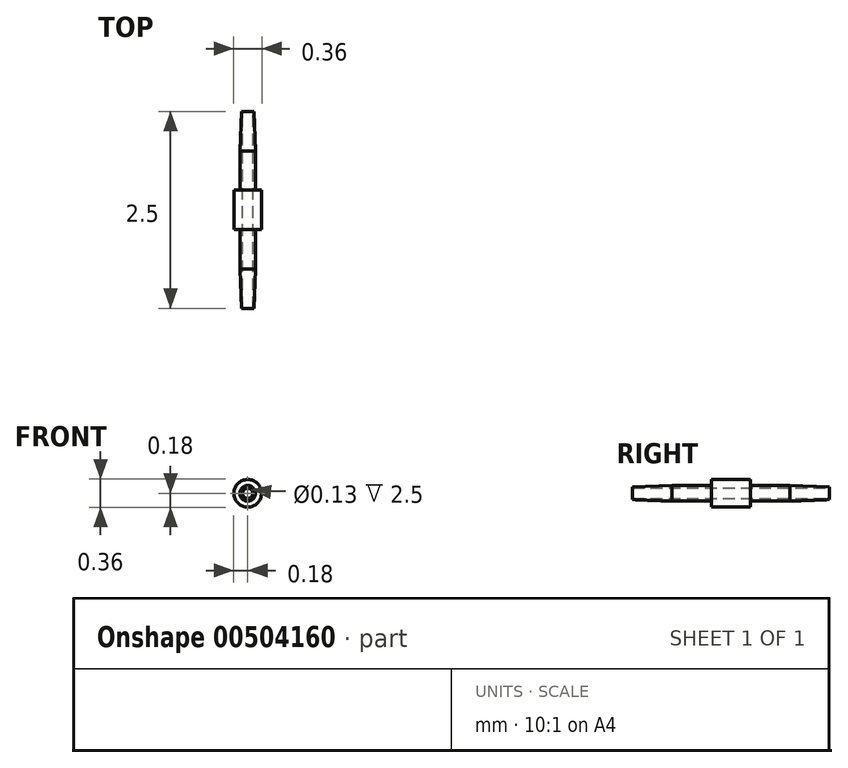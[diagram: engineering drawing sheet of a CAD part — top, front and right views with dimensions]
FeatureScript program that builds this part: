
annotation { "Feature Type Name" : "Feature", "Feature Type Description" : "" }
export const myFeature = defineFeature(function(context is Context, id is Id, definition is map)
    precondition{}
    {
        {
            var Q0;
            Q0=qCreatedBy(makeId("Front.planeOp"),FACE);
            var sketch = newSketch(context, id + "F0", { "sketchPlane" : qUnion([Q0])});
            skCircle(sketch, "E0", {"center": v(0, 0) * mm, "radius": 0.07 * mm});
            skCircle(sketch, "E1", {"center": v(0, 0) * mm, "radius": 0.1 * mm});
            skCircle(sketch, "E2", {"center": v(0, 0) * mm, "radius": 0.17 * mm});
            skSolve(sketch);
        }
        {
            var Q0;
            Q0=makeQuery(id+"F0.imprint","IMPRINT",FACE,{"disambiguationData":[TD([[makeQuery(id+"F0.imprint","IMPRINT",EDGE,{"derivedFrom":sQuery(id+"F0.wireOp",EDGE,"E1")}),-1.0]])]});
            var Q1;
            Q1=makeQuery(id+"F0.imprint","IMPRINT",FACE,{"disambiguationData":[TD([[makeQuery(id+"F0.imprint","IMPRINT",EDGE,{"derivedFrom":sQuery(id+"F0.wireOp",EDGE,"E0")}),-1.0]])]});
            extrude(context, id + "F1", {"entities" : qUnion([Q0, Q1]), "endBound" : BoundingType.SYMMETRIC, "depth" : 0.5 * mm});
        }
        {
            var Q0;
            Q0=makeQuery(id+"F0.imprint","IMPRINT",FACE,{"disambiguationData":[TD([[makeQuery(id+"F0.imprint","IMPRINT",EDGE,{"derivedFrom":sQuery(id+"F0.wireOp",EDGE,"E0")}),-1.0]])]});
            extrude(context, id + "F2", {"entities" : qUnion([Q0]), "operationType" : NewBodyOperationType.ADD, "endBound" : BoundingType.SYMMETRIC, "depth" : 1.5 * mm, "offsetDistance" : 25 * mm});
        }
        {
            var Q0;
            Q0=qCreatedBy(makeId("Right.planeOp"),FACE);
            var sketch = newSketch(context, id + "F3", { "sketchPlane" : qUnion([Q0])});
            skLineSegment(sketch, "E3", {"start": v(0, 0) * mm, "end": v(1.25, 0) * mm});
            skLineSegment(sketch, "E4", {"start": v(1.25, 0) * mm, "end": v(1.25, 0.07) * mm});
            skLineSegment(sketch, "E5", {"start": v(1.25, 0.07) * mm, "end": v(0.75, 0.07) * mm});
            skLineSegment(sketch, "E6", {"start": v(0.75, 0.07) * mm, "end": v(0.75, 0.1) * mm});
            skLineSegment(sketch, "E7", {"start": v(1.25, 0.07) * mm, "end": v(1.25, 0.08) * mm});
            skLineSegment(sketch, "E8", {"start": v(0.75, 0.1) * mm, "end": v(1.25, 0.08) * mm});
            skSolve(sketch);
        }
        {
            var Q0;
            Q0=makeQuery(id+"F3.imprint","IMPRINT",FACE,{"disambiguationData":[TD([[makeQuery(id+"F3.imprint","IMPRINT",EDGE,{"derivedFrom":sQuery(id+"F3.wireOp",EDGE,"E5")}),-1.0]])]});
            var Q1;
            Q1=sQuery(id+"F3.wireOp",EDGE,"E3");
            revolve(context, id + "F4", {"operationType" : NewBodyOperationType.ADD, "entities" : qUnion([Q0]), "axis" : qUnion([Q1]), "revolveType" : RevolveType.FULL});
        }
        {
            var Q0;
            Q0=makeQuery(id+"F1.opExtrude","SWEPT_BODY",BODY,{"disambiguationData":[OSD([sQuery(id+"F0.wireOp",EDGE,"E0"),sQuery(id+"F0.wireOp",EDGE,"E2")])]});
            var Q1;
            Q1=qCreatedBy(makeId("Front.planeOp"),FACE);
            mirror(context, id + "F5", {"operationType" : NewBodyOperationType.ADD, "entities" : qUnion([Q0]), "mirrorPlane" : qUnion([Q1])});
        }
    });
